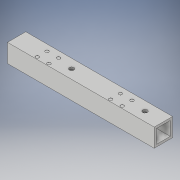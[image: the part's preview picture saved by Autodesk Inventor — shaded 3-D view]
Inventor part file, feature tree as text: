
AUTODESK INVENTOR PART (.ipt)
format: ipt  version: 2018 (Build 220112000, 112)  size: 133,120 bytes
history: native  units: in
note: dims shown in document units (in); Inventor stores cm internally (conversion verified against a paired STEP export)
features: extrude x3, sketch x3
ambient origin geometry x8: Origin, YZ Plane, XZ Plane, XY Plane, X Axis, Y Axis, Z Axis, Center Point
bodies: Solid1 (feature_tree)
feature tree (6):
  extrude  "Extrusion1"  Depth=1.0in
  extrude  "Extrusion2"  Depth=8.0in TaperAngle=0.0deg
  extrude  "Extrusion3"  Depth=0.01in TaperAngle=0.0deg
  sketch  "Sketch1"  dims[d0=1.0in d1=1.0in]
  sketch  "Sketch2"  dims[d2=0.125in d3=8.0in d4=0.0in]
  sketch  "Sketch3"  dims[d9=8.0in d10=0.0in d27=0.01in d28=0.0in d30=2.0in d31=0.25in d32=2.0in d33=0.25in d35=0.5in]
